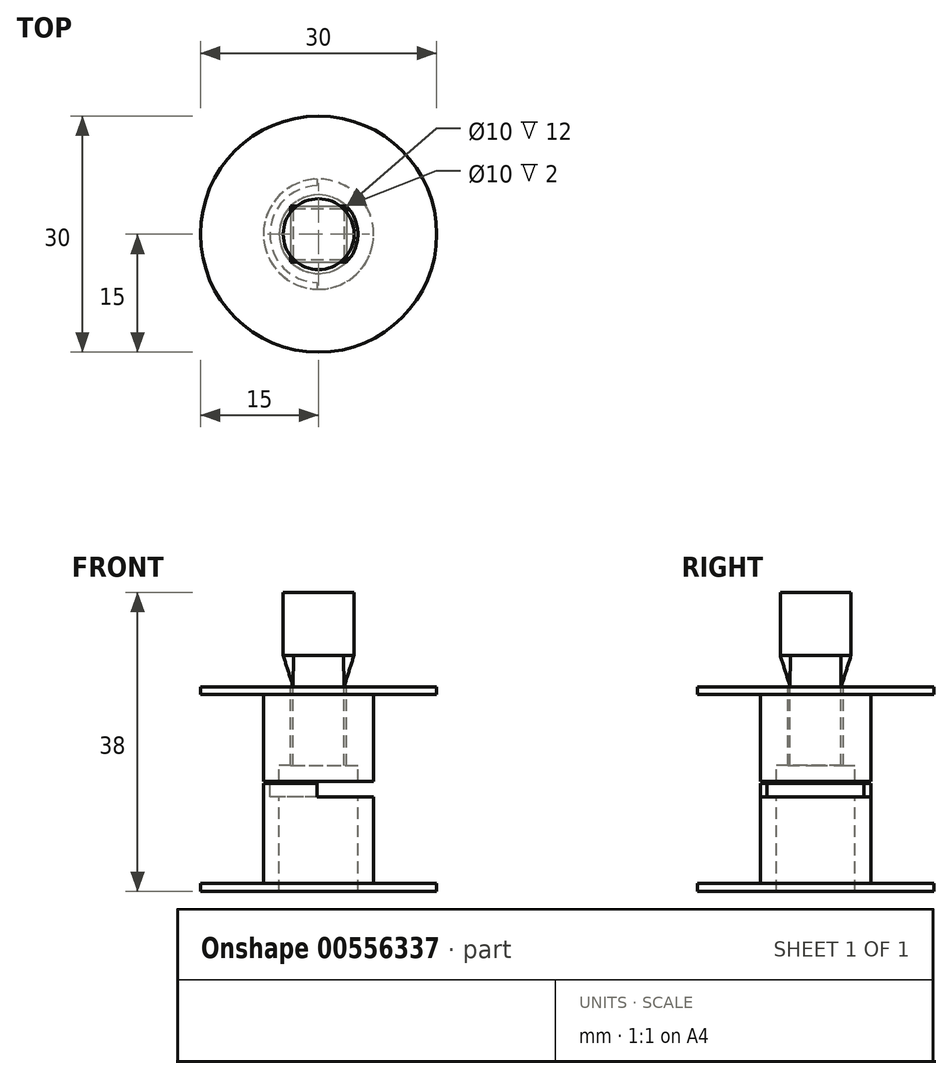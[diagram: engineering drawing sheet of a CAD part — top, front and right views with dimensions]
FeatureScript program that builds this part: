
annotation { "Feature Type Name" : "Feature", "Feature Type Description" : "" }
export const myFeature = defineFeature(function(context is Context, id is Id, definition is map)
    precondition{}
    {
        {
            var Q0;
            Q0=qCreatedBy(makeId("Front.planeOp"),FACE);
            var sketch = newSketch(context, id + "F0", { "sketchPlane" : qUnion([Q0])});
            skPoint(sketch, "E0.start.orphan", {"position": v(0, 12) * mm});
            skLineSegment(sketch, "E1", {"start": v(0, 12) * mm, "end": v(0, 0) * mm});
            skLineSegment(sketch, "E2", {"start": v(-15, 1) * mm, "end": v(-15, 0) * mm});
            skLineSegment(sketch, "E3.0", {"start": v(-5, 12) * mm, "end": v(-5, 1) * mm});
            skLineSegment(sketch, "E4.0", {"start": v(-7, 12) * mm, "end": v(-7, 1) * mm});
            skLineSegment(sketch, "E5.trimOffspring", {"start": v(-7, 1) * mm, "end": v(-15, 1) * mm});
            skLineSegment(sketch, "E6", {"start": v(-5, 1) * mm, "end": v(-5, 0) * mm});
            skLineSegment(sketch, "E7", {"start": v(-15, 0) * mm, "end": v(-5, 0) * mm});
            skLineSegment(sketch, "E8", {"start": v(-7, 12) * mm, "end": v(-5, 12) * mm});
            skLineSegment(sketch, "E9", {"start": v(0, 13) * mm, "end": v(-25.62, 13) * mm, "construction": true});
            skLineSegment(sketch, "E10.MirrorCS", {"start": v(-7, 14) * mm, "end": v(-5, 14) * mm});
            skLineSegment(sketch, "E11.MirrorCS", {"start": v(-15, 25) * mm, "end": v(-15, 26) * mm});
            skLineSegment(sketch, "E12.MirrorCS", {"start": v(-5, 25) * mm, "end": v(-5, 26) * mm});
            skLineSegment(sketch, "E13.MirrorCS", {"start": v(-5, 14) * mm, "end": v(-5, 25) * mm});
            skLineSegment(sketch, "E14.MirrorCS", {"start": v(-7, 14) * mm, "end": v(-7, 25) * mm});
            skLineSegment(sketch, "E15.MirrorCS", {"start": v(-15, 26) * mm, "end": v(-5, 26) * mm});
            skLineSegment(sketch, "E16.MirrorCS", {"start": v(-7, 25) * mm, "end": v(-15, 25) * mm});
            skSolve(sketch);
        }
        {
            var Q0;
            Q0=makeQuery(id+"F0.imprint","IMPRINT",FACE,{"disambiguationData":[TD([[makeQuery(id+"F0.imprint","IMPRINT",EDGE,{"derivedFrom":sQuery(id+"F0.wireOp",EDGE,"E2")}),1.0]])]});
            var Q1;
            Q1=makeQuery(id+"F0.imprint","IMPRINT",FACE,{"disambiguationData":[TD([[makeQuery(id+"F0.imprint","IMPRINT",EDGE,{"derivedFrom":sQuery(id+"F0.wireOp",EDGE,"E10.MirrorCS")}),1.0]])]});
            var Q2;
            Q2=sQuery(id+"F0.wireOp",EDGE,"E1");
            revolve(context, id + "F1", {"entities" : qUnion([Q0, Q1]), "axis" : qUnion([Q2]), "revolveType" : RevolveType.FULL});
        }
        {
            var Q0;
            Q0=qCreatedBy(makeId("Front.planeOp"),FACE);
            var sketch = newSketch(context, id + "F2", { "sketchPlane" : qUnion([Q0])});
            skLineSegment(sketch, "E17", {"start": v(-5, 12) * mm, "end": v(-5, 0) * mm});
            skLineSegment(sketch, "E18", {"start": v(5, 0) * mm, "end": v(5, 12) * mm});
            skLineSegment(sketch, "E19", {"start": v(-7, 12) * mm, "end": v(-7, 1) * mm});
            skLineSegment(sketch, "E20", {"start": v(7, 1) * mm, "end": v(7, 12) * mm});
            skLineSegment(sketch, "E21", {"start": v(5, 12) * mm, "end": v(7, 12) * mm});
            skLineSegment(sketch, "E22.bottom", {"start": v(-7, 12) * mm, "end": v(-6.16, 12) * mm});
            skLineSegment(sketch, "E22.top", {"start": v(-7, 13.75) * mm, "end": v(-6.16, 13.75) * mm});
            skLineSegment(sketch, "E22.left", {"start": v(-7, 12) * mm, "end": v(-7, 13.75) * mm});
            skLineSegment(sketch, "E22.right", {"start": v(-6.16, 12) * mm, "end": v(-6.16, 13.75) * mm});
            skLineSegment(sketch, "E23", {"start": v(5, 14) * mm, "end": v(7, 14) * mm});
            skLineSegment(sketch, "E24", {"start": v(-7, 14) * mm, "end": v(-5, 14) * mm});
            skLineSegment(sketch, "E25", {"start": v(-5, 14) * mm, "end": v(-5, 26) * mm});
            skLineSegment(sketch, "E26", {"start": v(5, 26) * mm, "end": v(5, 14) * mm});
            skLineSegment(sketch, "E27", {"start": v(-7, 14) * mm, "end": v(-7, 25) * mm});
            skLineSegment(sketch, "E28", {"start": v(7, 25) * mm, "end": v(7, 14) * mm});
            skLineSegment(sketch, "E29.bottom", {"start": v(-5, 14) * mm, "end": v(-5.83, 14) * mm});
            skLineSegment(sketch, "E29.top", {"start": v(-5, 12.25) * mm, "end": v(-5.83, 12.25) * mm});
            skLineSegment(sketch, "E29.left", {"start": v(-5, 14) * mm, "end": v(-5, 12.25) * mm});
            skLineSegment(sketch, "E29.right", {"start": v(-5.83, 14) * mm, "end": v(-5.83, 12.25) * mm});
            skLineSegment(sketch, "E30", {"start": v(0, 19.24) * mm, "end": v(0, 13.85) * mm});
            skLineSegment(sketch, "E31.bottom", {"start": v(7, 14) * mm, "end": v(6.16, 14) * mm});
            skLineSegment(sketch, "E31.top", {"start": v(7, 12.25) * mm, "end": v(6.16, 12.25) * mm});
            skLineSegment(sketch, "E31.left", {"start": v(7, 14) * mm, "end": v(7, 12.25) * mm});
            skLineSegment(sketch, "E31.right", {"start": v(6.16, 14) * mm, "end": v(6.16, 12.25) * mm});
            skLineSegment(sketch, "E32.bottom", {"start": v(5, 12) * mm, "end": v(5.83, 12) * mm});
            skLineSegment(sketch, "E32.top", {"start": v(5, 13.75) * mm, "end": v(5.83, 13.75) * mm});
            skLineSegment(sketch, "E32.left", {"start": v(5, 12) * mm, "end": v(5, 13.75) * mm});
            skLineSegment(sketch, "E32.right", {"start": v(5.83, 12) * mm, "end": v(5.83, 13.75) * mm});
            skSolve(sketch);
        }
        {
            var Q0;
            Q0=makeQuery(id+"F2.imprint","IMPRINT",FACE,{"disambiguationData":[TD([[makeQuery(id+"F2.imprint","IMPRINT",EDGE,{"derivedFrom":sQuery(id+"F2.wireOp",EDGE,"E29.bottom")}),1.0]])]});
            var Q1;
            Q1=makeQuery(id+"F2.imprint","IMPRINT",FACE,{"disambiguationData":[TD([[makeQuery(id+"F2.imprint","IMPRINT",EDGE,{"derivedFrom":sQuery(id+"F2.wireOp",EDGE,"E22.bottom")}),1.0]])]});
            var Q2;
            Q2=makeQuery(id+"F2.imprint","IMPRINT",FACE,{"disambiguationData":[TD([[makeQuery(id+"F2.imprint","IMPRINT",EDGE,{"derivedFrom":sQuery(id+"F2.wireOp",EDGE,"E32.bottom")}),1.0]])]});
            var Q3;
            Q3=makeQuery(id+"F2.imprint","IMPRINT",FACE,{"disambiguationData":[TD([[makeQuery(id+"F2.imprint","IMPRINT",EDGE,{"derivedFrom":sQuery(id+"F2.wireOp",EDGE,"E31.bottom")}),1.0]])]});
            var Q4;
            Q4=sQuery(id+"F2.wireOp",EDGE,"E30");
            revolve(context, id + "F3", {"operationType" : NewBodyOperationType.ADD, "entities" : qUnion([Q0, Q1, Q2, Q3]), "axis" : qUnion([Q4]), "revolveType" : RevolveType.SYMMETRIC, "angle" : 179 * degree});
        }
        {
            var Q0;
            Q0=makeQuery(id+"F1.opRevolve","SWEPT_FACE",FACE,{"disambiguationData":[OSD([sQuery(id+"F0.wireOp",EDGE,"E15.MirrorCS")])]});
            var sketch = newSketch(context, id + "F4", { "sketchPlane" : qUnion([Q0])});
            skLineSegment(sketch, "E33.bottom", {"start": v(-3.54, 3.54) * mm, "end": v(3.54, 3.54) * mm});
            skLineSegment(sketch, "E33.top", {"start": v(-3.54, -3.54) * mm, "end": v(3.54, -3.54) * mm});
            skLineSegment(sketch, "E33.left", {"start": v(-3.54, 3.54) * mm, "end": v(-3.54, -3.54) * mm});
            skLineSegment(sketch, "E33.right", {"start": v(3.54, 3.54) * mm, "end": v(3.54, -3.54) * mm});
            skPoint(sketch, "E33.middle", {"position": v(0, 0) * mm});
            skCircle(sketch, "E34", {"center": v(0, 0) * mm, "radius": 5 * mm});
            skSolve(sketch);
        }
        {
            var Q0;
            {var subQ0=sQuery(id+"F4.wireOp",EDGE,"E33.left");Q0=makeQuery(id+"F4.imprint","IMPRINT",FACE,{"disambiguationData":[TD([[makeQuery(id+"F4.imprint","IMPRINT",EDGE,{"derivedFrom":subQ0}),-1.0]])]});}
            var Q1;
            {var subQ0=sQuery(id+"F4.wireOp",EDGE,"E33.bottom");Q1=makeQuery(id+"F4.imprint","IMPRINT",FACE,{"disambiguationData":[TD([[makeQuery(id+"F4.imprint","IMPRINT",EDGE,{"derivedFrom":subQ0}),1.0]])]});}
            var Q2;
            {var subQ0=sQuery(id+"F4.wireOp",EDGE,"E33.right");Q2=makeQuery(id+"F4.imprint","IMPRINT",FACE,{"disambiguationData":[TD([[makeQuery(id+"F4.imprint","IMPRINT",EDGE,{"derivedFrom":subQ0}),1.0]])]});}
            var Q3;
            {var subQ0=sQuery(id+"F4.wireOp",EDGE,"E33.top");Q3=makeQuery(id+"F4.imprint","IMPRINT",FACE,{"disambiguationData":[TD([[makeQuery(id+"F4.imprint","IMPRINT",EDGE,{"derivedFrom":subQ0}),-1.0]])]});}
            extrude(context, id + "F5", {"entities" : qUnion([Q0, Q1, Q2, Q3]), "operationType" : NewBodyOperationType.ADD, "oppositeDirection" : true, "depth" : 10 * mm, "offsetDistance" : 25 * mm});
        }
        {
            var Q0;
            {var subQ0=sQuery(id+"F4.wireOp",EDGE,"E34");Q0=makeQuery(id+"F5.boolean.opBoolean","MERGE",FACE,{"derivedFrom":[makeQuery(id+"F1.opRevolve","SWEPT_FACE",FACE,{"disambiguationData":[OSD([sQuery(id+"F0.wireOp",EDGE,"E15.MirrorCS")])]}),makeQuery(id+"F5.opExtrude","CAP_FACE",FACE,{"disambiguationData":[OSD([sQuery(id+"F4.wireOp",EDGE,"E33.bottom"),subQ0])],"isStart":true}),makeQuery(id+"F5.opExtrude","CAP_FACE",FACE,{"disambiguationData":[OSD([sQuery(id+"F4.wireOp",EDGE,"E33.top"),subQ0])],"isStart":true}),makeQuery(id+"F5.opExtrude","CAP_FACE",FACE,{"disambiguationData":[OSD([sQuery(id+"F4.wireOp",EDGE,"E33.left"),subQ0])],"isStart":true}),makeQuery(id+"F5.opExtrude","CAP_FACE",FACE,{"disambiguationData":[OSD([sQuery(id+"F4.wireOp",EDGE,"E33.right"),subQ0])],"isStart":true})]});}
            cPlane(context, id + "F6", {"entities" : qUnion([Q0]), "cplaneType" : CPlaneType.OFFSET, "offset" : 4 * mm, "width" : 150 * mm, "height" : 150 * mm});
        }
        {
            var Q0;
            Q0=qCreatedBy(id+"F6.planeOp",FACE);
            var sketch = newSketch(context, id + "F7", { "sketchPlane" : qUnion([Q0])});
            skCircle(sketch, "E35", {"center": v(0, 0) * mm, "radius": 4.5 * mm});
            skSolve(sketch);
        }
        {
            var Q0;
            {var subQ0=sQuery(id+"F4.wireOp",EDGE,"E34");Q0=makeQuery(id+"F5.boolean.opBoolean","MERGE",FACE,{"derivedFrom":[makeQuery(id+"F1.opRevolve","SWEPT_FACE",FACE,{"disambiguationData":[OSD([sQuery(id+"F0.wireOp",EDGE,"E15.MirrorCS")])]}),makeQuery(id+"F5.opExtrude","CAP_FACE",FACE,{"disambiguationData":[OSD([sQuery(id+"F4.wireOp",EDGE,"E33.bottom"),subQ0])],"isStart":true}),makeQuery(id+"F5.opExtrude","CAP_FACE",FACE,{"disambiguationData":[OSD([sQuery(id+"F4.wireOp",EDGE,"E33.top"),subQ0])],"isStart":true}),makeQuery(id+"F5.opExtrude","CAP_FACE",FACE,{"disambiguationData":[OSD([sQuery(id+"F4.wireOp",EDGE,"E33.left"),subQ0])],"isStart":true}),makeQuery(id+"F5.opExtrude","CAP_FACE",FACE,{"disambiguationData":[OSD([sQuery(id+"F4.wireOp",EDGE,"E33.right"),subQ0])],"isStart":true})]});}
            var sketch = newSketch(context, id + "F8", { "sketchPlane" : qUnion([Q0])});
            skLineSegment(sketch, "E36.bottom", {"start": v(-3.24, 3.24) * mm, "end": v(3.24, 3.24) * mm});
            skLineSegment(sketch, "E36.top", {"start": v(-3.24, -3.24) * mm, "end": v(3.24, -3.24) * mm});
            skLineSegment(sketch, "E36.left", {"start": v(-3.24, 3.24) * mm, "end": v(-3.24, -3.24) * mm});
            skLineSegment(sketch, "E36.right", {"start": v(3.24, 3.24) * mm, "end": v(3.24, -3.24) * mm});
            skPoint(sketch, "E36.middle", {"position": v(0, 0) * mm});
            skSolve(sketch);
        }
        {
            var Q0;
            Q0=makeQuery(id+"F8.imprint","IMPRINT",FACE,{"disambiguationData":[TD([[makeQuery(id+"F8.imprint","IMPRINT",EDGE,{"derivedFrom":sQuery(id+"F8.wireOp",EDGE,"E36.bottom")}),-1.0]])]});
            var Q1;
            Q1=makeQuery(id+"F7.imprint","IMPRINT",FACE,{"disambiguationData":[TD([[makeQuery(id+"F7.imprint","IMPRINT",EDGE,{"derivedFrom":sQuery(id+"F7.wireOp",EDGE,"E35")}),1.0]])]});
            loft(context, id + "F9", {"sheetProfilesArray" : [{ "sheetProfileEntities" : qUnion([Q0]) }, { "sheetProfileEntities" : qUnion([Q1]) }]});
        }
        {
            var Q0;
            Q0=makeQuery(id+"F9.opLoft","CAP_FACE",FACE,{"disambiguationData":[OSD([makeQuery(id+"F8.imprint","IMPRINT",FACE,{"disambiguationData":[TD([[makeQuery(id+"F8.imprint","IMPRINT",EDGE,{"derivedFrom":sQuery(id+"F8.wireOp",EDGE,"E36.bottom")}),-1.0]])]})])],"isStart":true});
            extrude(context, id + "F10", {"entities" : qUnion([Q0]), "operationType" : NewBodyOperationType.ADD, "depth" : 10 * mm, "offsetDistance" : 25 * mm});
        }
        {
            var Q0;
            Q0=makeQuery(id+"F9.opLoft","CAP_FACE",FACE,{"disambiguationData":[OSD([makeQuery(id+"F7.imprint","IMPRINT",FACE,{"disambiguationData":[TD([[makeQuery(id+"F7.imprint","IMPRINT",EDGE,{"derivedFrom":sQuery(id+"F7.wireOp",EDGE,"E35")}),1.0]])]})])],"isStart":true});
            extrude(context, id + "F11", {"entities" : qUnion([Q0]), "operationType" : NewBodyOperationType.ADD, "depth" : (12 - 4) * mm, "offsetDistance" : 25 * mm});
        }
        {
            var Q0;
            Q0=qCreatedBy(makeId("Front.planeOp"),FACE);
            var sketch = newSketch(context, id + "F12", { "sketchPlane" : qUnion([Q0])});
            skLineSegment(sketch, "E37.bottom", {"start": v(-0.2, 14) * mm, "end": v(0.2, 14) * mm});
            skLineSegment(sketch, "E37.top", {"start": v(-0.2, 12) * mm, "end": v(0.2, 12) * mm});
            skLineSegment(sketch, "E37.left", {"start": v(-0.2, 14) * mm, "end": v(-0.2, 12) * mm});
            skLineSegment(sketch, "E37.right", {"start": v(0.2, 14) * mm, "end": v(0.2, 12) * mm});
            skPoint(sketch, "E37.middle", {"position": v(0, 13) * mm});
            skSolve(sketch);
        }
        {
            var Q0;
            Q0 = qSketchRegion(id + "F12", true);
            extrude(context, id + "F13", {"entities" : qUnion([Q0]), "operationType" : NewBodyOperationType.REMOVE, "endBound" : BoundingType.SYMMETRIC, "oppositeDirection" : true, "depth" : 25 * mm, "offsetDistance" : 25 * mm});
        }
    });
